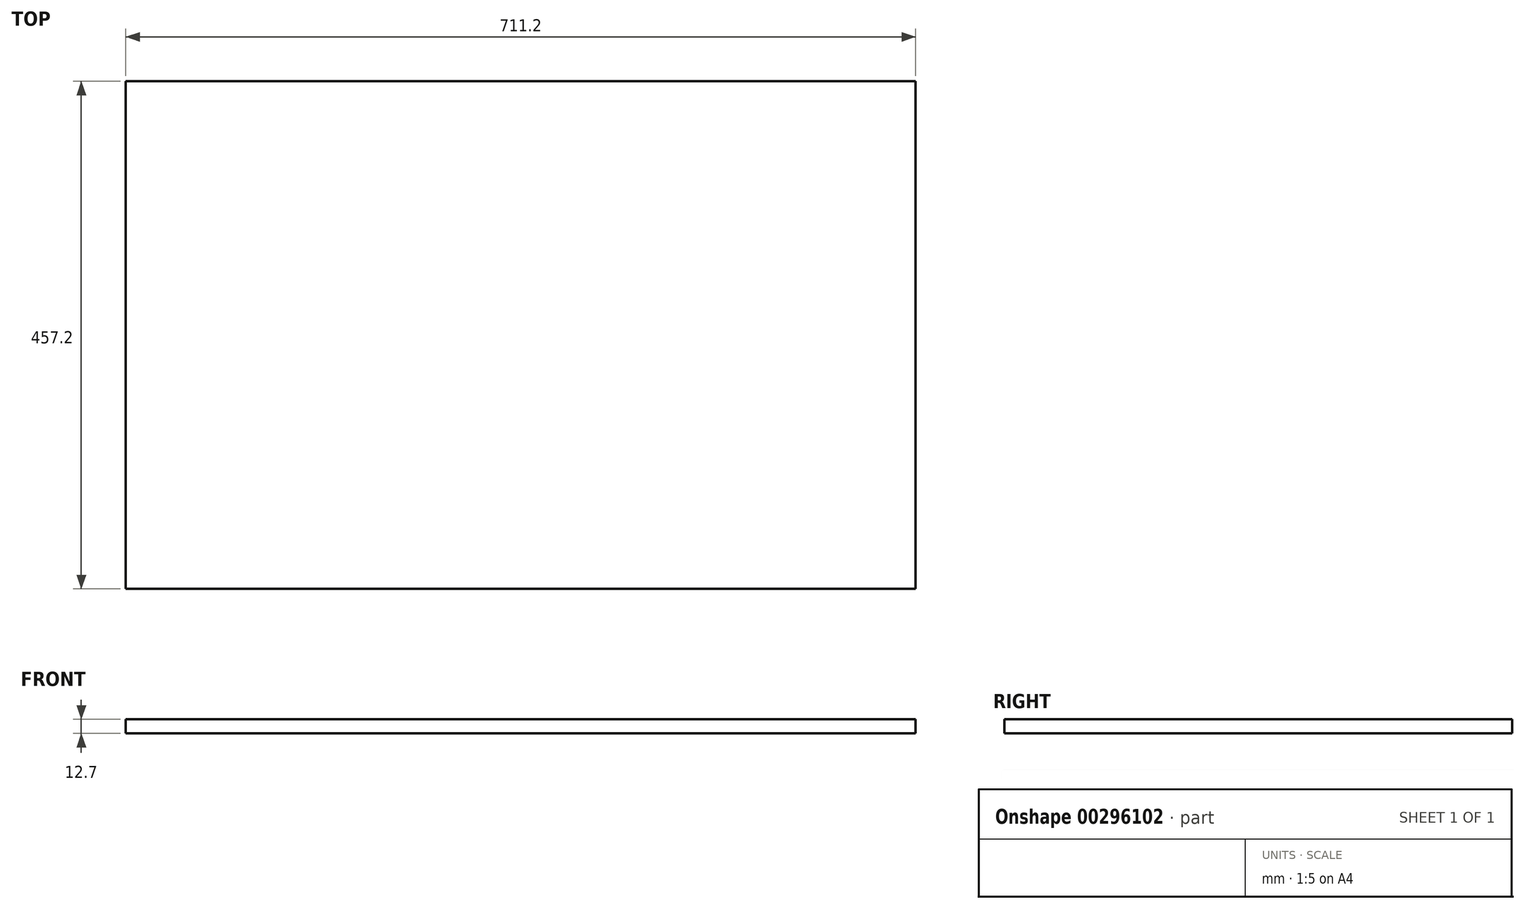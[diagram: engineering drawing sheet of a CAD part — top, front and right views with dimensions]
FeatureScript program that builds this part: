
annotation { "Feature Type Name" : "Feature", "Feature Type Description" : "" }
export const myFeature = defineFeature(function(context is Context, id is Id, definition is map)
    precondition{}
    {
        {
            var Q0;
            Q0=qCreatedBy(makeId("Top.planeOp"),FACE);
            var sketch = newSketch(context, id + "F0", { "sketchPlane" : qUnion([Q0])});
            skLineSegment(sketch, "E0.bottom", {"start": v(355.6, 228.6) * mm, "end": v(-355.6, 228.6) * mm});
            skLineSegment(sketch, "E0.top", {"start": v(355.6, -228.6) * mm, "end": v(-355.6, -228.6) * mm});
            skLineSegment(sketch, "E0.left", {"start": v(355.6, 228.6) * mm, "end": v(355.6, -228.6) * mm});
            skLineSegment(sketch, "E0.right", {"start": v(-355.6, 228.6) * mm, "end": v(-355.6, -228.6) * mm});
            skPoint(sketch, "E0.middle", {"position": v(0, 0) * mm});
            skSolve(sketch);
        }
        {
            var Q0;
            Q0=makeQuery(id+"F0.imprint","IMPRINT",FACE,{"disambiguationData":[TD([[makeQuery(id+"F0.imprint","IMPRINT",EDGE,{"derivedFrom":sQuery(id+"F0.wireOp",EDGE,"E0.bottom")}),1.0]])]});
            extrude(context, id + "F1", {"entities" : qUnion([Q0]), "depth" : 12.7 * mm});
        }
    });
